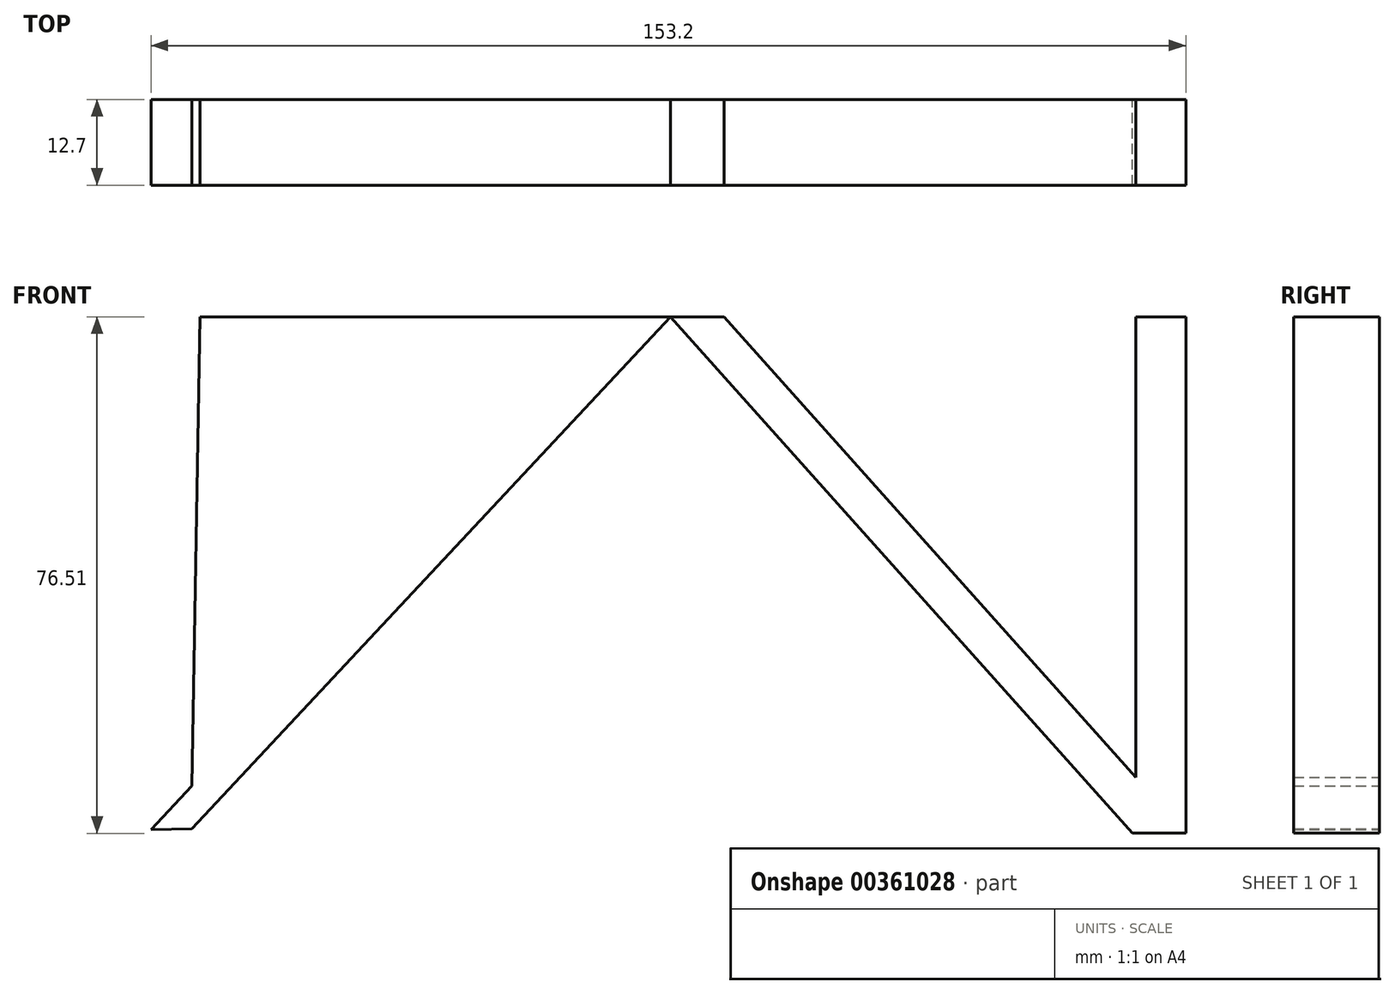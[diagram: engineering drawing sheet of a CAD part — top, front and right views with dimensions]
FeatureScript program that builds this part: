
annotation { "Feature Type Name" : "Feature", "Feature Type Description" : "" }
export const myFeature = defineFeature(function(context is Context, id is Id, definition is map)
    precondition{}
    {
        {
            var Q0;
            Q0=qCreatedBy(makeId("Front.planeOp"),FACE);
            var sketch = newSketch(context, id + "F0", { "sketchPlane" : qUnion([Q0])});
            skLineSegment(sketch, "E0", {"start": v(-76.87, -75.97) * mm, "end": v(-5.95, 0) * mm});
            skLineSegment(sketch, "E1", {"start": v(-5.95, 0) * mm, "end": v(0, 0) * mm});
            skLineSegment(sketch, "E2", {"start": v(0, 0) * mm, "end": v(-70.8, -75.84) * mm});
            skLineSegment(sketch, "E3", {"start": v(-70.8, -75.84) * mm, "end": v(-76.87, -75.97) * mm});
            skLineSegment(sketch, "E4", {"start": v(0, 0) * mm, "end": v(68.39, -76.5) * mm});
            skLineSegment(sketch, "E5", {"start": v(68.39, -76.5) * mm, "end": v(76.33, -76.5) * mm});
            skLineSegment(sketch, "E6", {"start": v(76.33, -76.5) * mm, "end": v(7.94, 0) * mm});
            skLineSegment(sketch, "E7", {"start": v(7.94, 0) * mm, "end": v(0, 0) * mm});
            skLineSegment(sketch, "E8", {"start": v(76.33, -76.5) * mm, "end": v(76.33, 0) * mm});
            skLineSegment(sketch, "E9", {"start": v(76.33, 0) * mm, "end": v(68.93, 0) * mm});
            skLineSegment(sketch, "E10", {"start": v(68.93, 0) * mm, "end": v(68.93, -68.23) * mm});
            skLineSegment(sketch, "E11", {"start": v(-76.87, -75.97) * mm, "end": v(-76.87, 0) * mm});
            skLineSegment(sketch, "E12", {"start": v(-76.87, 0) * mm, "end": v(-69.65, 0) * mm});
            skLineSegment(sketch, "E13", {"start": v(-69.65, 0) * mm, "end": v(-70.8, -69.47) * mm});
            skLineSegment(sketch, "E14", {"start": v(-70.8, -69.47) * mm, "end": v(-5.95, 0) * mm});
            skLineSegment(sketch, "E15", {"start": v(-76.87, 0) * mm, "end": v(76.33, 0) * mm});
            skSolve(sketch);
        }
        {
            var Q0;
            {var subQ5=sQuery(id+"F0.wireOp",EDGE,"E4");Q0=makeQuery(id+"F0.imprint","IMPRINT",FACE,{"disambiguationData":[TD([[makeQuery(id+"F0.imprint","IMPRINT",EDGE,{"derivedFrom":subQ5}),1.0]])]});}
            var Q1;
            Q1=makeQuery(id+"F0.imprint","IMPRINT",FACE,{"disambiguationData":[TD([[makeQuery(id+"F0.imprint","IMPRINT",EDGE,{"derivedFrom":sQuery(id+"F0.wireOp",EDGE,"E0")}),-1.0]])]});
            var Q2;
            {var subQ0=sQuery(id+"F0.wireOp",EDGE,"E8");Q2=makeQuery(id+"F0.imprint","IMPRINT",FACE,{"disambiguationData":[TD([[makeQuery(id+"F0.imprint","IMPRINT",EDGE,{"derivedFrom":subQ0}),1.0]])]});}
            var Q3;
            Q3=makeQuery(id+"F0.imprint","IMPRINT",FACE,{"disambiguationData":[TD([[makeQuery(id+"F0.imprint","IMPRINT",EDGE,{"derivedFrom":sQuery(id+"F0.wireOp",EDGE,"E0")}),1.0]])]});
            var Q4;
            Q4=makeQuery(id+"F0.imprint","IMPRINT",FACE,{"disambiguationData":[TD([[makeQuery(id+"F0.imprint","IMPRINT",EDGE,{"derivedFrom":sQuery(id+"F0.wireOp",EDGE,"E0")}),-1.0]])]});
            var Q5;
            Q5=makeQuery(id+"F0.imprint","IMPRINT",FACE,{"disambiguationData":[TD([[makeQuery(id+"F0.imprint","IMPRINT",EDGE,{"derivedFrom":sQuery(id+"F0.wireOp",EDGE,"E0")}),1.0]])]});
            var Q6;
            {var subQ5=sQuery(id+"F0.wireOp",EDGE,"E4");Q6=makeQuery(id+"F0.imprint","IMPRINT",FACE,{"disambiguationData":[TD([[makeQuery(id+"F0.imprint","IMPRINT",EDGE,{"derivedFrom":subQ5}),1.0]])]});}
            var Q7;
            {var subQ0=sQuery(id+"F0.wireOp",EDGE,"E8");Q7=makeQuery(id+"F0.imprint","IMPRINT",FACE,{"disambiguationData":[TD([[makeQuery(id+"F0.imprint","IMPRINT",EDGE,{"derivedFrom":subQ0}),1.0]])]});}
            extrude(context, id + "F1", {"entities" : qUnion([Q0, Q1, Q2, Q3, Q4, Q5, Q6, Q7]), "depth" : 12.7 * mm});
        }
    });
